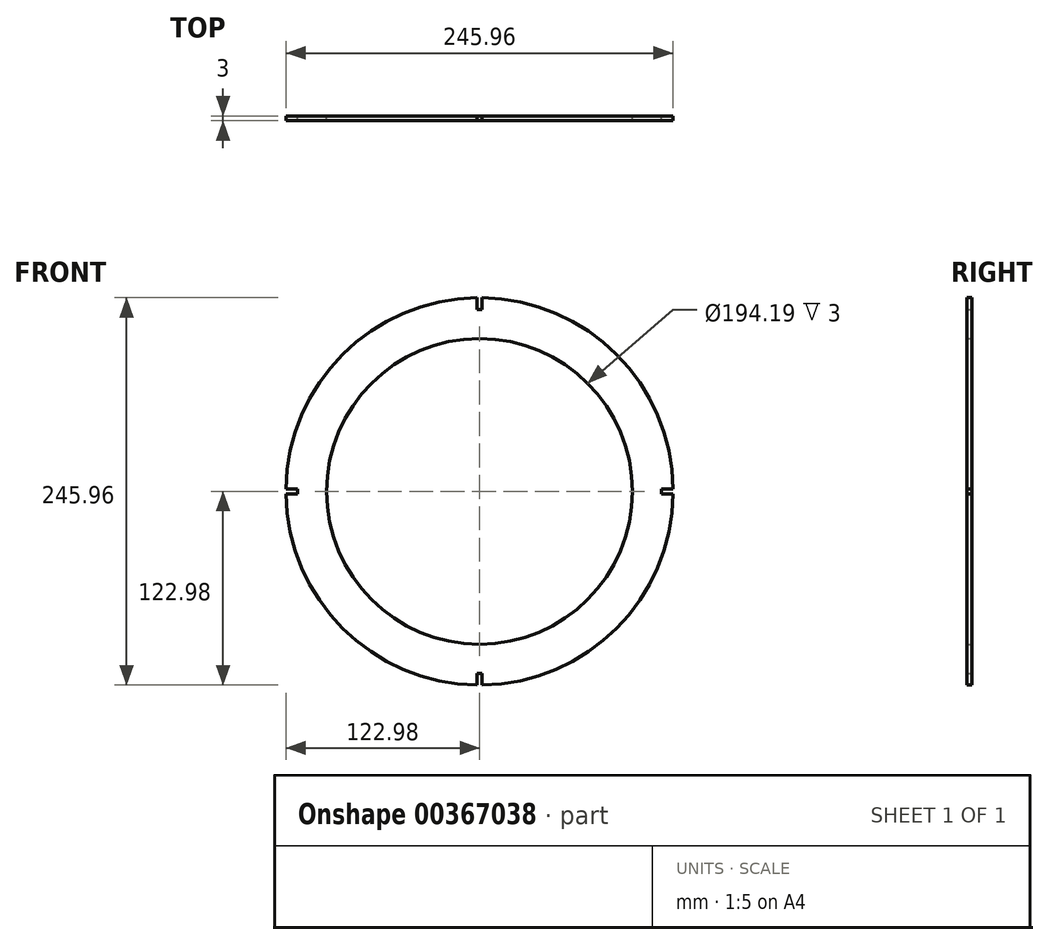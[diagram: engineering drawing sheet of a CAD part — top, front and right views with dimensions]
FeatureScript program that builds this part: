
annotation { "Feature Type Name" : "Feature", "Feature Type Description" : "" }
export const myFeature = defineFeature(function(context is Context, id is Id, definition is map)
    precondition{}
    {
        {
            var Q0;
            Q0=qCreatedBy(makeId("Front.planeOp"),FACE);
            var sketch = newSketch(context, id + "F0", { "sketchPlane" : qUnion([Q0])});
            skArc(sketch, "E0", {"start": v(-1.5, 122.98) * mm, "mid": v(-86.96, 86.96) * mm, "end": v(-122.98, 1.5) * mm});
            skPoint(sketch, "E1.center.orphan", {"position": v(0, 127.62) * mm});
            skCircle(sketch, "E2", {"center": v(0, 0) * mm, "radius": 97.1 * mm});
            skPoint(sketch, "E3.end.orphan", {"position": v(0, 97.1) * mm});
            skLineSegment(sketch, "E4.top", {"start": v(1.5, 115.49) * mm, "end": v(-1.5, 115.49) * mm});
            skLineSegment(sketch, "E4.left", {"start": v(1.5, 122.98) * mm, "end": v(1.5, 115.49) * mm});
            skLineSegment(sketch, "E4.right", {"start": v(-1.5, 122.98) * mm, "end": v(-1.5, 115.49) * mm});
            skPoint(sketch, "E4.middle", {"position": v(0, 122.99) * mm});
            skPoint(sketch, "E4.bottom.start.orphan", {"position": v(1.5, 130.49) * mm});
            skPoint(sketch, "E5.orphan", {"position": v(-1.5, 130.49) * mm});
            skPoint(sketch, "E6.middle", {"position": v(97.1, 0) * mm});
            skPoint(sketch, "E7.orphan", {"position": v(89.6, -1.4) * mm});
            skPoint(sketch, "E6.right.start.orphan", {"position": v(89.6, 1.4) * mm});
            skPoint(sketch, "E8.orphan", {"position": v(104.6, -1.4) * mm});
            skPoint(sketch, "E6.left.start.orphan", {"position": v(104.6, 1.4) * mm});
            skLineSegment(sketch, "E9.bottom", {"start": v(122.98, 1.5) * mm, "end": v(115.49, 1.5) * mm});
            skLineSegment(sketch, "E9.top", {"start": v(122.98, -1.5) * mm, "end": v(115.49, -1.5) * mm});
            skLineSegment(sketch, "E9.right", {"start": v(115.49, 1.5) * mm, "end": v(115.49, -1.5) * mm});
            skPoint(sketch, "E9.middle", {"position": v(122.99, 0) * mm});
            skPoint(sketch, "E9.left.start.orphan", {"position": v(130.49, 1.5) * mm});
            skPoint(sketch, "E10.orphan", {"position": v(130.49, -1.5) * mm});
            skArc(sketch, "E11.trimOffspring", {"start": v(122.98, 1.5) * mm, "mid": v(86.96, 86.96) * mm, "end": v(1.5, 122.98) * mm});
            skLineSegment(sketch, "E12.bottom", {"start": v(1.5, -115.49) * mm, "end": v(-1.5, -115.49) * mm});
            skLineSegment(sketch, "E12.left", {"start": v(1.5, -115.49) * mm, "end": v(1.5, -122.98) * mm});
            skLineSegment(sketch, "E12.right", {"start": v(-1.5, -115.49) * mm, "end": v(-1.5, -122.98) * mm});
            skPoint(sketch, "E12.middle", {"position": v(0, -122.99) * mm});
            skArc(sketch, "E13.trimOffspring", {"start": v(1.5, -122.98) * mm, "mid": v(86.96, -86.96) * mm, "end": v(122.98, -1.5) * mm});
            skPoint(sketch, "E12.top.end.orphan", {"position": v(-1.5, -130.49) * mm});
            skPoint(sketch, "E12.top.start.orphan", {"position": v(1.5, -130.49) * mm});
            skLineSegment(sketch, "E14.bottom", {"start": v(-115.49, 1.5) * mm, "end": v(-122.98, 1.5) * mm});
            skLineSegment(sketch, "E14.top", {"start": v(-115.49, -1.5) * mm, "end": v(-122.98, -1.5) * mm});
            skLineSegment(sketch, "E14.left", {"start": v(-115.49, 1.5) * mm, "end": v(-115.49, -1.5) * mm});
            skPoint(sketch, "E14.middle", {"position": v(-122.99, 0) * mm});
            skPoint(sketch, "E14.right.start.orphan", {"position": v(-130.49, 1.5) * mm});
            skArc(sketch, "E15.trimOffspring", {"start": v(-122.98, -1.5) * mm, "mid": v(-86.96, -86.96) * mm, "end": v(-1.5, -122.98) * mm});
            skPoint(sketch, "E16.orphan", {"position": v(-130.49, -1.5) * mm});
            skPoint(sketch, "E17.end.orphan", {"position": v(86.96, 86.96) * mm});
            skPoint(sketch, "E18.end.orphan", {"position": v(-86.96, -86.96) * mm});
            skPoint(sketch, "E19.trimOffspring.end.orphan", {"position": v(-86.96, 86.96) * mm});
            skPoint(sketch, "E20.start.orphan", {"position": v(86.96, -86.96) * mm});
            skSolve(sketch);
        }
        {
            var Q0;
            Q0 = qSketchRegion(id + "F0", true);
            extrude(context, id + "F1", {"entities" : qUnion([Q0]), "depth" : 3 * mm});
        }
    });
